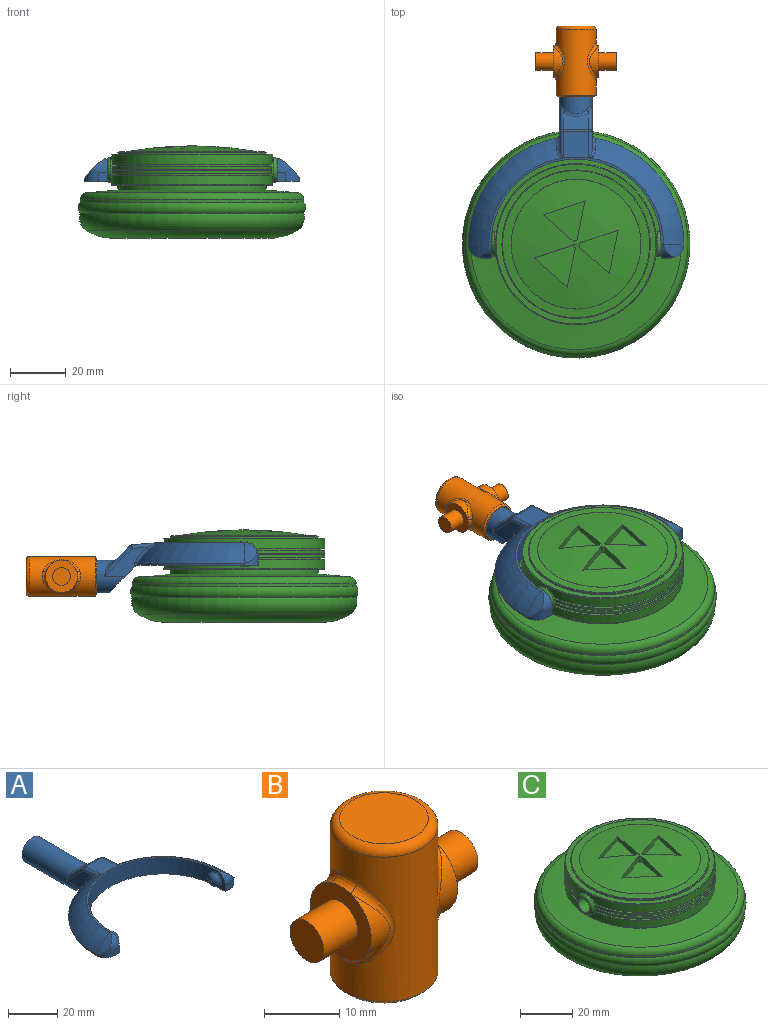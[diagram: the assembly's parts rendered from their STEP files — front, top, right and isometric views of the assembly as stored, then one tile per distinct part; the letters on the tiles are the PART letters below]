
ASSEMBLY  parts=3 mates=2
PART A: 48 faces, bbox 77.3x80.8x18.2 mm
  f0: plane 11.99x9.83mm, normal (0,-0.71,-0.71), area 141.5mm2, adj f1,f2,f9,f30,f43,f46
  f1: plane 15.39x10.49mm, normal (-1,0,0), area 63.5mm2, adj f0,f30,f32,f36,f46,f47
  f2: plane 15.39x10.49mm, normal (1,0,0), area 63.5mm2, adj f0,f30,f34,f39,f43,f44
  f3: plane 9.14x6.37mm, normal (0,0.71,0.71), area 67.6mm2, adj f35,f36,f39,f40
  f4: cylinder r=38.61mm len=37.99mm, axis (0,0,-1), area 42.6mm2, adj f6,f9,f17,f46,f47
  f5: torus R=19.3mm, axis (0,0,-1), area 507.8mm2, adj f10,f11,f12,f29,f42,f44
  f6: torus R=19.3mm, axis (0,0,-1), area 507.8mm2, adj f4,f11,f15,f28,f45,f47
  f7: cylinder r=30.48mm len=60.96mm, axis (0,0,-1), area 746.6mm2, adj f8,f9,f11,f14,f21,f24
  f8: plane 8.13x5.08mm, normal (-1,0,0), area 19.9mm2, adj f7,f9,f13,f19,f24
  f9: plane 77.22x43.73mm, normal (0,0,-1), area 956.2mm2, adj f0,f4,f7,f8,f10,f13,f14,f16
  f10: cylinder r=38.61mm len=37.99mm, axis (0,0,-1), area 42.6mm2, adj f5,f9,f20,f43,f44
  f11: plane 62.55x30.95mm, normal (0,0,1), area 75mm2, adj f5,f6,f7,f18,f19,f27
  f12: cylinder r=22.71mm len=7.33mm, axis (0,1,0), area 24.8mm2, adj f5,f19,f20
  f13: plane 3.05x3.05mm, normal (0,-1,0), area 9.3mm2, adj f8,f9,f19,f20
  f14: plane 8.13x5.08mm, normal (1,0,0), area 19.9mm2, adj f7,f9,f16,f18,f21
  f15: cylinder r=22.71mm len=7.33mm, axis (0,1,0), area 24.8mm2, adj f6,f17,f18
  f16: plane 3.05x3.05mm, normal (0,-1,0), area 9.3mm2, adj f9,f14,f17,f18
  f17: cylinder r=5.08mm len=5.08mm, axis (0,0,-1), area 21.9mm2, adj f4,f9,f15,f16,f18
  f18: cylinder r=5.08mm len=5.08mm, axis (-1,0,0), area 21.9mm2, adj f11,f14,f15,f16,f17
  f19: cylinder r=5.08mm len=5.08mm, axis (-1,0,0), area 21.9mm2, adj f8,f11,f12,f13,f20
  f20: cylinder r=5.08mm len=5.08mm, axis (0,0,-1), area 21.9mm2, adj f9,f10,f12,f13,f19
  f21: cylinder r=3.17mm len=6.35mm, axis (-1,0,0), area 12.7mm2, adj f7,f14,f23
  f22: plane 1.27x1.27mm, normal (1,0,0), area 1.3mm2, adj f23
  f23: torus R=0.64mm, axis (1,0,0), area 56.5mm2, adj f21,f22
  f24: cylinder r=3.17mm len=6.35mm, axis (1,0,0), area 12.7mm2, adj f7,f8,f26
  f25: plane 1.27x1.27mm, normal (-1,0,0), area 1.3mm2, adj f26
  f26: torus R=0.64mm, axis (-1,0,0), area 56.5mm2, adj f24,f25
  f27: plane 9.86x9.36mm, normal (0,0.09,1), area 85.6mm2, adj f11,f28,f29,f32,f34,f35,f42,f45
  f28: plane 1.04x0.17mm, normal (0,-1,0), area 0mm2, adj f6,f27,f45
  f29: plane 1.04x0.17mm, normal (0,-1,0), area 0mm2, adj f5,f27,f42
  f30: cylinder r=5.84mm len=33.01mm, axis (0,-1,0), area 1029.7mm2, adj f0,f1,f2,f31,f38,f40,f41
  f31: plane 11.68x11.68mm, normal (0,1,0), area 107.2mm2, adj f30
  f32: cylinder r=1.27mm len=9.13mm, axis (0,-1,0.09), area 14.4mm2, adj f1,f27,f33,f45
  f33: sphere r=1.27mm, area 1.5mm2, adj f32,f35,f36
  f34: cylinder r=1.27mm len=9.13mm, axis (0,1,-0.09), area 14.4mm2, adj f2,f27,f37,f42
  f35: cylinder r=1.27mm len=9.14mm, axis (-1,0,0), area 8.1mm2, adj f3,f27,f33,f37
  f36: cylinder r=1.27mm len=10.91mm, axis (0,-0.71,0.71), area 23.1mm2, adj f1,f3,f33,f38
  f37: sphere r=1.27mm, area 1.5mm2, adj f34,f35,f39
  f38: bspline ~4.55x2.75mm, area 2.3mm2, adj f30,f36,f40
  f39: cylinder r=1.27mm len=10.91mm, axis (0,0.71,-0.71), area 23.1mm2, adj f2,f3,f37,f41
  f40: bspline ~9.14x2.56mm, area 10.7mm2, adj f3,f30,f38,f41
  f41: bspline ~5.23x3.53mm, area 2.3mm2, adj f30,f39,f40
  f42: bspline ~4.62x3.14mm, area 5.2mm2, adj f5,f27,f29,f34,f44
  f43: cylinder r=1.27mm len=1.74mm, axis (0,0,-1), area 1.9mm2, adj f0,f2,f9,f10,f44
  f44: bspline ~8.6x7.86mm, area 11.9mm2, adj f2,f5,f10,f42,f43
  f45: bspline ~4.62x3.14mm, area 5.2mm2, adj f6,f27,f28,f32,f47
  f46: cylinder r=1.27mm len=1.74mm, axis (0,0,-1), area 1.9mm2, adj f0,f1,f4,f9,f47
  f47: bspline ~8.6x7.86mm, area 11.9mm2, adj f1,f4,f6,f45,f46
PART B: 25 faces, bbox 28.9x15.5x25.4 mm
  f0: cylinder r=5.71mm len=10.81mm, axis (-1,0,0), area 26.2mm2, adj f5,f15
  f1: cylinder r=5.71mm len=10.81mm, axis (-1,0,0), area 26.2mm2, adj f8,f11
  f2: cylinder r=7.14mm len=23.5mm, axis (0,0,-1), area 763.2mm2, adj f9,f10,f11,f12,f13,f14,f15,f16
  f3: plane 11.75x11.75mm, normal (0,0,1), area 108.4mm2, adj f17
  f4: plane 13.02x13.02mm, normal (0,0,-1), area 16.3mm2, adj f22,f24
  f5: plane 11.46x11.46mm, normal (1,0,0), area 70.9mm2, adj f0,f6,f13,f16,f18
  f6: cylinder r=5.71mm len=10.81mm, axis (-1,0,0), area 26.2mm2, adj f5,f14
  f7: cylinder r=5.71mm len=10.81mm, axis (-1,0,0), area 26.2mm2, adj f8,f10
  f8: plane 11.46x11.46mm, normal (-1,0,0), area 70.9mm2, adj f1,f7,f9,f12,f20
  f9: bspline ~4.64x1.73mm, area 6.5mm2, adj f2,f8,f10,f11
  f10: bspline ~13.62x4.91mm, area 20.7mm2, adj f2,f7,f9,f12
  f11: bspline ~13.6x4.87mm, area 20.7mm2, adj f1,f2,f9,f12
  f12: bspline ~4.64x1.73mm, area 6.5mm2, adj f2,f8,f10,f11
  f13: bspline ~4.64x1.73mm, area 6.5mm2, adj f2,f5,f14,f15
  f14: bspline ~13.62x4.91mm, area 20.7mm2, adj f2,f6,f13,f16
  f15: bspline ~13.6x4.87mm, area 20.7mm2, adj f0,f2,f13,f16
  f16: bspline ~4.64x1.73mm, area 6.5mm2, adj f2,f5,f14,f15
  f17: torus R=5.87mm, axis (0,0,1), area 83.8mm2, adj f2,f3
  f18: cylinder r=3.17mm len=6.35mm, axis (-1,0,0), area 126.7mm2, adj f5,f19
  f19: plane 6.35x6.35mm, normal (1,0,0), area 31.7mm2, adj f18
  f20: cylinder r=3.17mm len=6.35mm, axis (1,0,0), area 126.7mm2, adj f8,f21
  f21: plane 6.35x6.35mm, normal (-1,0,0), area 31.7mm2, adj f20
  f22: cylinder r=6.1mm len=22.86mm, axis (0,0,-1), area 875.6mm2, adj f4,f23
  f23: plane 12.19x12.19mm, normal (0,0,-1), area 116.7mm2, adj f22
  f24: cone r=7.14mm half-angle=45deg, axis (0,0,1), area 38.5mm2, adj f2,f4
PART C: 64 faces, bbox 88.9x88.9x33 mm
  f0: sphere r=135.39mm, area 1385.3mm2, adj f48,f49,f50,f51,f52,f54,f55,f56
  f1: cylinder r=28.87mm len=57.73mm, axis (0,0,-1), area 595.8mm2, adj f19,f20,f39,f40,f46
  f2: cylinder r=28.87mm len=57.06mm, axis (0,0,-1), area 77.8mm2, adj f8,f14,f39,f40
  f3: cylinder r=28.87mm len=57.06mm, axis (0,0,-1), area 77.8mm2, adj f7,f13,f39,f40
  f4: cylinder r=28.87mm len=57.06mm, axis (0,0,-1), area 77.8mm2, adj f12,f22,f39,f40
  f5: cylinder r=28.87mm len=57.06mm, axis (0,0,-1), area 77.8mm2, adj f11,f21,f39,f40
  f6: cylinder r=28.87mm len=57.73mm, axis (0,0,-1), area 595.8mm2, adj f15,f16,f39,f40,f45
  f7: plane 57.01x24.31mm, normal (0,0,1), area 101mm2, adj f3,f10,f39,f40
  f8: plane 57.01x24.31mm, normal (0,0,1), area 101mm2, adj f2,f9,f39,f40
  f9: cylinder r=27.6mm len=54.44mm, axis (0,0,-1), area 49.2mm2, adj f8,f12,f39,f40
  f10: cylinder r=27.6mm len=54.44mm, axis (0,0,-1), area 49.2mm2, adj f7,f11,f39,f40
  f11: plane 57.01x24.31mm, normal (0,0,-1), area 101mm2, adj f5,f10,f39,f40
  f12: plane 57.01x24.31mm, normal (0,0,-1), area 101mm2, adj f4,f9,f39,f40
  f13: plane 57.06x24.48mm, normal (0,0,-1), area 101.4mm2, adj f3,f18,f39,f40
  f14: plane 57.06x24.48mm, normal (0,0,-1), area 101.4mm2, adj f2,f17,f39,f40
  f15: plane 57.13x24.71mm, normal (0,0,1), area 102mm2, adj f6,f18,f39,f40
  f16: plane 57.13x24.71mm, normal (0,0,1), area 102mm2, adj f6,f17,f39,f40
  f17: cylinder r=27.6mm len=54.56mm, axis (0,0,-1), area 49.6mm2, adj f14,f16,f39,f40
  f18: cylinder r=27.6mm len=54.56mm, axis (0,0,-1), area 49.6mm2, adj f13,f15,f39,f40
  f19: plane 57.13x24.71mm, normal (0,0,-1), area 102mm2, adj f1,f24,f39,f40
  f20: plane 57.13x24.71mm, normal (0,0,-1), area 102mm2, adj f1,f23,f39,f40
  f21: plane 57.06x24.48mm, normal (0,0,1), area 101.4mm2, adj f5,f24,f39,f40
  f22: plane 57.06x24.48mm, normal (0,0,1), area 101.4mm2, adj f4,f23,f39,f40
  f23: cylinder r=27.6mm len=54.56mm, axis (0,0,-1), area 49.6mm2, adj f20,f22,f39,f40
  f24: cylinder r=27.6mm len=54.56mm, axis (0,0,-1), area 49.6mm2, adj f19,f21,f39,f40
  f25: plane 35.35x35.35mm, normal (0,0,-1), area 981.4mm2, adj f26
  f26: torus R=19.79mm, axis (0,0,-1), area 1365.7mm2, adj f25,f27
  f27: torus R=28.4mm, axis (0,0,-1), area 3558.3mm2, adj f26,f28
  f28: torus R=35.03mm, axis (0,0,-1), area 1794.3mm2, adj f27,f29
  f29: torus R=37.73mm, axis (0,0,-1), area 1070.2mm2, adj f28,f30
  f30: cylinder r=40.07mm len=80.14mm, axis (0,0,-1), area 213.4mm2, adj f29,f37
  f31: cone r=26.58mm half-angle=85deg, axis (0,0,-1), area 2265.9mm2, adj f32,f37
  f32: cylinder r=26.58mm len=53.16mm, axis (0,0,-1), area 265.1mm2, adj f31,f33
  f33: plane 57.23x57.23mm, normal (0,0,-1), area 352.3mm2, adj f32,f45
  f34: plane 57.23x57.23mm, normal (0,0,1), area 352.3mm2, adj f35,f46
  f35: cylinder r=26.58mm len=53.16mm, axis (0,0,-1), area 92.3mm2, adj f34,f47
  f36: cone r=26.58mm half-angle=87deg, axis (0,0,-1), area 477.5mm2, adj f47,f48
  f37: torus R=37.53mm, axis (0,0,1), area 928.9mm2, adj f30,f31
  f38: plane 6.6x6.6mm, normal (1,0,0), area 2.6mm2, adj f43,f44
  f39: cylinder r=4.57mm len=9.14mm, axis (-1,0,0), area 20.2mm2, adj f1,f2,f3,f4,f5,f6,f7,f8
  f40: cylinder r=4.57mm len=9.14mm, axis (-1,0,0), area 20.2mm2, adj f1,f2,f3,f4,f5,f6,f7,f8
  f41: plane 6.6x6.6mm, normal (-1,0,0), area 2.6mm2, adj f42,f44
  f42: torus R=3.3mm, axis (1,0,0), area 51.5mm2, adj f40,f41
  f43: torus R=3.3mm, axis (1,0,0), area 51.5mm2, adj f38,f39
  f44: cylinder r=3.17mm len=60.96mm, axis (1,0,0), area 1216.1mm2, adj f38,f41
  f45: torus R=28.61mm, axis (0,0,1), area 72.1mm2, adj f6,f33
  f46: torus R=28.61mm, axis (0,0,-1), area 72.1mm2, adj f1,f34
  f47: torus R=26.33mm, axis (0,0,1), area 64.2mm2, adj f35,f36
  f48: torus R=23.29mm, axis (0,0,1), area 4.5mm2, adj f0,f36
  f49: cylinder r=1.27mm len=2.53mm, axis (0,0,1), area 3.4mm2, adj f0,f50,f52,f53
  f50: plane 13.87x4.59mm, normal (0.31,-0.95,0), area 32.2mm2, adj f0,f49,f51,f53
  f51: plane 11.85x10.56mm, normal (0.67,0.75,0), area 28mm2, adj f0,f50,f52,f53
  f52: plane 14.3x2.96mm, normal (-0.98,0.2,0), area 32.2mm2, adj f0,f49,f51,f53
  f53: plane 15.15x14.81mm, normal (0,0,1), area 108.3mm2, adj f49,f50,f51,f52
  f54: plane 13.87x4.59mm, normal (0.31,-0.95,0), area 32.2mm2, adj f0,f55,f57,f58
  f55: cylinder r=1.27mm len=2.53mm, axis (0,0,1), area 3.4mm2, adj f0,f54,f56,f58
  f56: plane 10.91x9.71mm, normal (0.67,0.75,0), area 32.2mm2, adj f0,f55,f57,f58
  f57: plane 15.55x3.22mm, normal (-0.98,0.2,0), area 28mm2, adj f0,f54,f56,f58
  f58: plane 15.55x14.12mm, normal (0,0,1), area 108.3mm2, adj f54,f55,f56,f57
  f59: plane 10.91x9.71mm, normal (0.67,0.75,0), area 32.2mm2, adj f0,f60,f62,f63
  f60: cylinder r=1.27mm len=2.53mm, axis (0,0,1), area 3.4mm2, adj f0,f59,f61,f63
  f61: plane 14.3x2.96mm, normal (-0.98,0.2,0), area 32.2mm2, adj f0,f60,f62,f63
  f62: plane 15.07x4.99mm, normal (0.31,-0.95,0), area 28mm2, adj f0,f59,f61,f63
  f63: plane 15.07x14.7mm, normal (0,0,1), area 108.3mm2, adj f59,f60,f61,f62
PLACE A t=(32.34,27.52,20.85)mm
PLACE B rot(axis=(-1,0,0),90deg) t=(32.34,80.3,16.88)mm
PLACE C t=(32.34,27.52,33.52)mm
MATE revolute A.f24 <-> C.f39  axis (-1,0,0) through (62.82,27.52,24.92)mm
MATE revolute B.f2 <-> A.f30  axis (0,-1,0) through (32.34,103.16,16.88)mm
